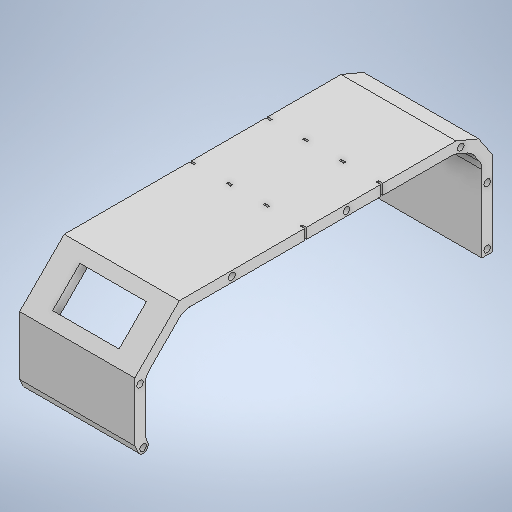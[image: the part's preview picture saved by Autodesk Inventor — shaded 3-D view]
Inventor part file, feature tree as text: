
AUTODESK INVENTOR PART (.ipt)
format: ipt  version: 2025.2 (Build 292293000, 293)  size: 906,240 bytes
history: native  units: mm
features: sketch x14, extrude x13, projected_geometry x5, chamfer x4, pattern_linear x3, fillet x1
ambient origin geometry x8: Origin, YZ Plane, XZ Plane, XY Plane, X Axis, Y Axis, Z Axis, Center Point
bodies: Solid1 (feature_tree)
feature tree (40):
  extrude  "Extrusion1"  Depth=180.0mm
  extrude  "Extrusion16"  Depth=76.5mm
  extrude  "Extrusion17"  Depth=117.0mm
  chamfer  "Chamfer1"  Distance=77.4mm
  chamfer  "Chamfer2"  [1 undecoded]
  chamfer  "Chamfer3"  [1 undecoded]
  extrude  "Extrusion18"  Depth=20.0mm TaperAngle=45.0deg
  extrude  "Extrusion19"  TaperAngle=0.0deg  [1 undecoded]
  sketch  "Sketch20"  dims[d11=45.0deg]
  extrude  "Extrusion20"  Depth=7.05mm
  pattern_linear  "Rectangular Pattern4"  Spacing1=3.525mm  [1 undecoded]
  extrude  "Extrusion21"  Depth=3.0mm
  pattern_linear  "Rectangular Pattern5"  Spacing1=0.0mm  [1 undecoded]
  extrude  "Extrusion22"  Depth=10.0mm
  pattern_linear  "Rectangular Pattern6"  Spacing1=4.45mm  [1 undecoded]
  extrude  "Extrusion23"  Depth=8.0mm TaperAngle=0.0deg
  extrude  "Extrusion25"  Depth=10.0mm
  extrude  "Extrusion24"  Depth=8.0mm TaperAngle=0.0deg
  extrude  "Extrusion26"  Depth=10.0mm
  chamfer  "Chamfer4"  Distance=75.6mm
  extrude  "Extrusion27"  Depth=50.0mm
  fillet  "Fillet4"  Radius=25.0mm
  sketch  "Sketch1"  dims[d0=100.0mm d1=180.0mm]
  sketch  "Sketch15"  dims[d4=7.15585mm d5=117.0mm]
  projected_geometry  "Projected Loop7"
  sketch  "Sketch16"  dims[d7=7.15585mm]
  sketch  "Sketch17"  dims[d9=30.0mm]
  projected_geometry  "Projected Loop8"
  sketch  "Sketch19"  dims[d10=50.0mm]
  sketch  "Sketch21"  dims[d12=38.0mm d13=77.4mm d14=0.0mm d79=0.0mm d80=0.0mm]
  sketch  "Sketch22"  dims[d81=31.5mm d82=0.0mm d83=0.0mm]
  sketch  "Sketch23"  dims[d84=30.0mm d85=2.0mm d86=45.0deg d87=20.0mm d88=2.0mm d89=45.0deg]
  projected_geometry  "Projected Loop9"
  sketch  "Sketch Rectangular Pattern1"  dims[d2=90.0mm d3=76.5mm]
  sketch  "Sketch24"  dims[d90=10.0mm d91=2.0mm d92=45.0deg d93=0.0mm d94=0.0mm]
  projected_geometry  "Projected Loop10"
  sketch  "Sketch25"  dims[d95=7.05mm d96=7.05mm]
  projected_geometry  "Projected Loop11"
  sketch  "Sketch26"  dims[d97=10.0mm d98=0.0mm]
  sketch  "Sketch27"  dims[d99=3.0mm d100=3.525mm d102=3.0mm d103=0.0mm d104=0.0mm d105=100.0mm d107=4.45mm d108=8.0mm d109=0.0mm d110=100.0mm d112=8.0mm d113=0.0mm d114=100.0mm d116=75.6mm d117=50.0mm d118=25.0mm d119=1.3mm d120=3.0mm d121=40.0mm d123=24.8mm d124=10.0mm d126=10.0mm d128=0.0mm d129=0.0mm d130=44.7mm d131=26.0mm d132=0.0mm d133=0.0mm d134=3.0mm d135=3.0mm d136=4.75mm d137=0.0mm d138=4.75mm d139=0.0mm d140=1.0mm d141=2.0mm d142=45.0deg d143=4.75mm d144=0.0mm d147=10.0mm]
note: 6 required parameter values undecoded (feature->parameter linkage not recoverable at this tier; creation-order binding heuristic only, values carry confidence <= 0.55)
